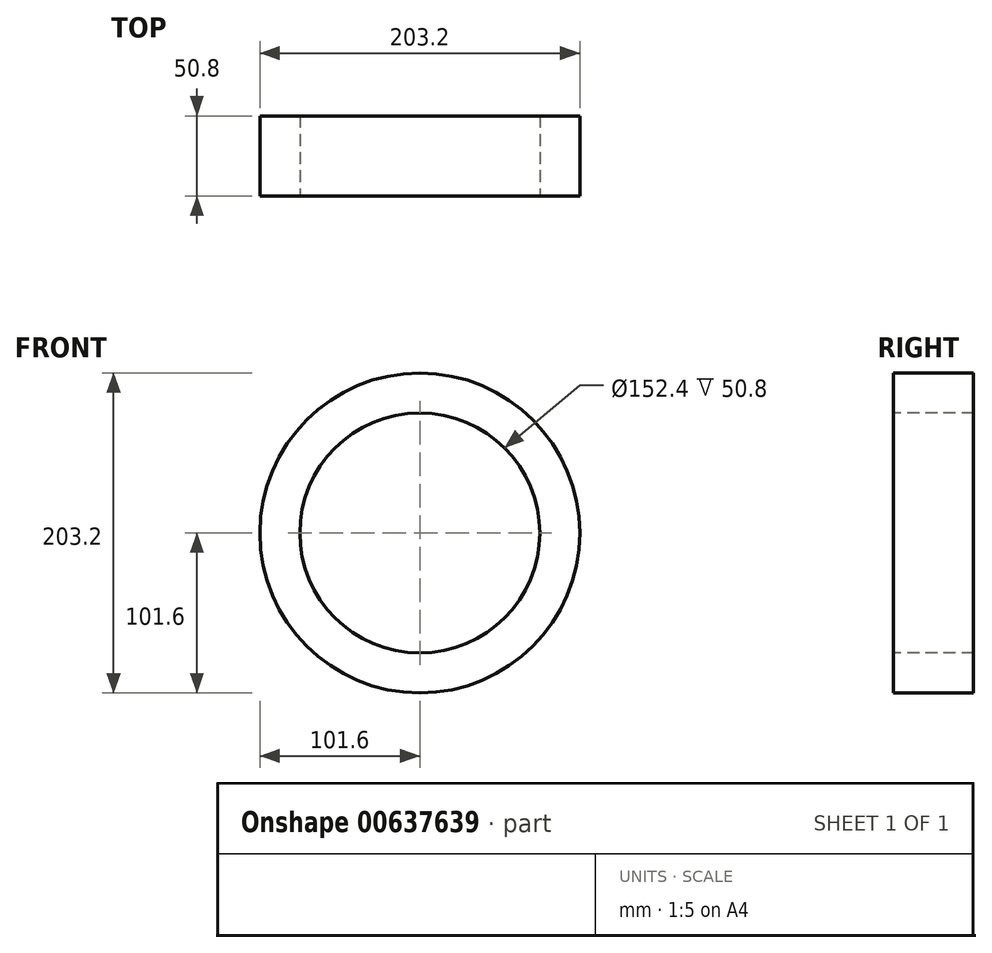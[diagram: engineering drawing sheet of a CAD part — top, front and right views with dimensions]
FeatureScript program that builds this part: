
annotation { "Feature Type Name" : "Feature", "Feature Type Description" : "" }
export const myFeature = defineFeature(function(context is Context, id is Id, definition is map)
    precondition{}
    {
        {
            var Q0;
            Q0=qCreatedBy(makeId("Top.planeOp"),FACE);
            var sketch = newSketch(context, id + "F0", { "sketchPlane" : qUnion([Q0])});
            skLineSegment(sketch, "E0.bottom", {"start": v(76.2, 0) * mm, "end": v(101.6, 0) * mm});
            skLineSegment(sketch, "E0.top", {"start": v(76.2, 50.8) * mm, "end": v(101.6, 50.8) * mm});
            skLineSegment(sketch, "E0.left", {"start": v(76.2, 0) * mm, "end": v(76.2, 50.8) * mm});
            skLineSegment(sketch, "E0.right", {"start": v(101.6, 0) * mm, "end": v(101.6, 50.8) * mm});
            skLineSegment(sketch, "E1", {"start": v(0, 0) * mm, "end": v(0, 143.57) * mm, "construction": true});
            skSolve(sketch);
        }
        {
            var Q0;
            Q0=makeQuery(id+"F0.imprint","IMPRINT",FACE,{"disambiguationData":[TD([[makeQuery(id+"F0.imprint","IMPRINT",EDGE,{"derivedFrom":sQuery(id+"F0.wireOp",EDGE,"E0.bottom")}),1.0]])]});
            var Q1;
            Q1=sQuery(id+"F0.wireOp",EDGE,"E1");
            revolve(context, id + "F1", {"entities" : qUnion([Q0]), "axis" : qUnion([Q1]), "revolveType" : RevolveType.FULL});
        }
    });
